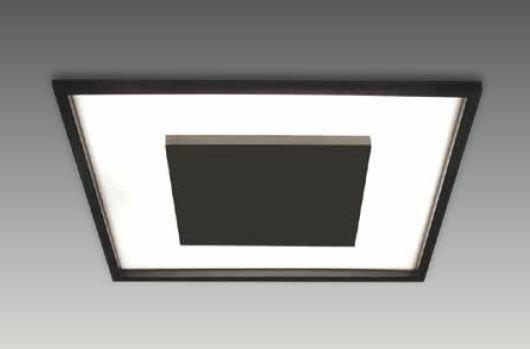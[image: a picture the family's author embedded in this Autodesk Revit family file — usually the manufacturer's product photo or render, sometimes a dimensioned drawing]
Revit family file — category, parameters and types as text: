
# Revit family: DG 2035 OPK
name_source: partatom
category: Lighting Fixtures
revit_build: Autodesk Revit 2017 (Build: 20160225_1515(x64)
units: mm (PartAtom-declared; Revit-internal decimal feet)

## family parameters
Always vertical = Yes
Cut with Voids When Loaded = No
Host = Ceiling
Light Source = Yes
OmniClass Number = 23.80.70.11
OmniClass Title = Luminaries for Internal Lighting
Part Type = Normal
Room Calculation Point = No
Round Connector Dimension = Use Diameter
Shared = No

## types (2) — shared parameters
Color Filter = 16777215
Dimming Lamp Color Temperature Shift = <None>
Emit Shape Visible in Rendering = Yes
Emit from Rectangle Length = 310 mm  [stored 1.01706 ft]
Emit from Rectangle Width = 310 mm  [stored 1.01706 ft]
Light Source Symbol Size = 610 mm
Manufacturer = ARLIGHT
Type Image = DG 2035 OPK.JPG
Wattage Comments = 28

## type names (no varying parameters)
- DGOPK.3535.28.30
- DGOPK.3535.28.40

note: [stored X ft] marks values corroborated as IEEE doubles in the binary element streams (Revit-internal decimal feet)

## geometry (parser evidence)
native form markers: Sweep x2
no freeform markers — native parametric forms only
